# Revit family: result
name_source: partatom
category: Generic Models
revit_build: Autodesk Revit 2015 (Build: 20140903_1530(x64)
units: mm (PartAtom-declared; Revit-internal decimal feet)

## types (1)
- Default
    BIMobject category = Compound Units
    BIMobject category code = sanitary-compound-units
    BIMobject main category = Sanitary
    BIMobject main category code = sanitary
    Brand url = http://www.duravit.com
    Edition number = 1
    GTIN code = https://4063382166067
    IFC Classification = Furnishing Element
    Installation instructions = https://duravit-public-assets.s3.eu-central-1.amazonaws.com
    Manufacturer name = DURAVIT
    Masterformat 2014 Code = 12 50 00
    Masterformat 2014 Description = Furniture
    Material main = Wood
    NBS Reference Code = 35-75-08
    NBS Reference Description = Bathroom Cabinets
    OmniClass Code = 23-19 31 17 11
    OmniClass Description = Bathroom Units
    Product Guid = 5e0c2d55-6da2-474b-b7c4-7bec76b4d7c7
    Product SKU = d-neo-vanity-unit-wall-mounted-de4958
    Product data url = https://bimobject.com
    Product family = D-Neo
    Product group = Vanity unit wall-mounted
    Product name = DE4958 D-Neo Vanity unit wall-mounted
    Product url = https://duravit-public-assets.s3.eu-central-1.amazonaws.com
    QR code = http://bimobject.com
    Technical description = https://duravit-public-assets.s3.eu-central-1.amazonaws.com
    UNSPSC Code = 56
    Uniclass 1.4 Code = L8241
    Uniclass 1.4 Description = Bathroom cabinets
    Uniclass 2.0 Code = PR-35-75-08
    Uniclass 2.0 Description = Bathroom Cabinets
    Uniclass 2015 Code = Pr_40_30_78_05
    Uniclass 2015 Name = Bathroom furniture
    Uniformat II Code = E2010
    Uniformat II Description = Fixed Furnishings

## geometry (parser evidence)
native form markers: Sweep x3
no freeform markers — native parametric forms only
